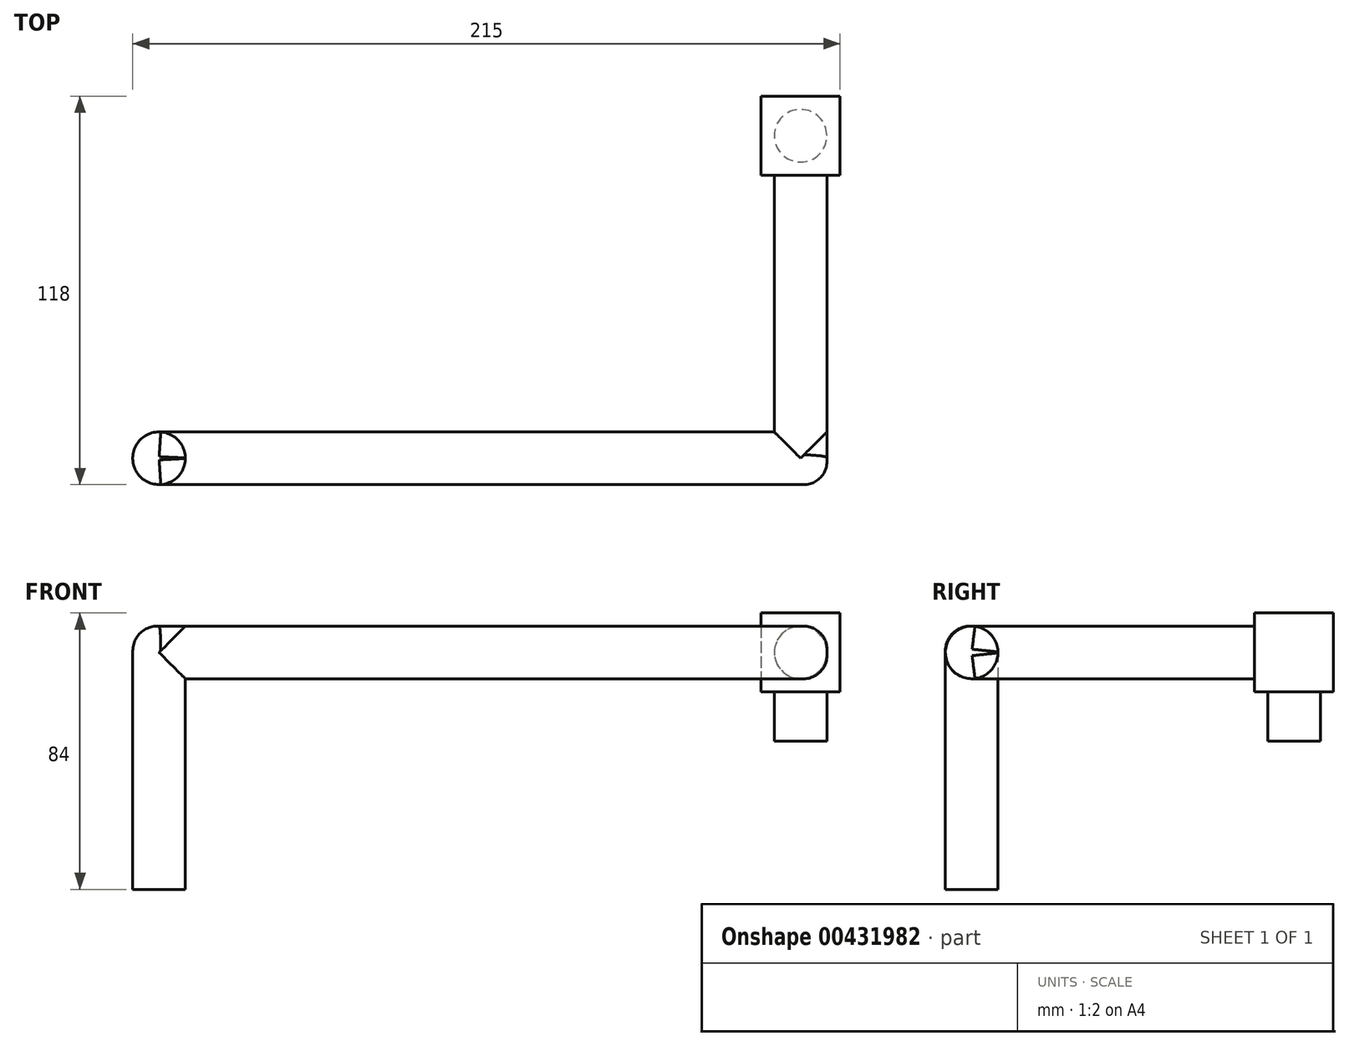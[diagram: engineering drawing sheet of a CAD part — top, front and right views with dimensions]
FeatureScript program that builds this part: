
annotation { "Feature Type Name" : "Feature", "Feature Type Description" : "" }
export const myFeature = defineFeature(function(context is Context, id is Id, definition is map)
    precondition{}
    {
        {
            var Q0;
            Q0=qCreatedBy(makeId("Top.planeOp"),FACE);
            var sketch = newSketch(context, id + "F0", { "sketchPlane" : qUnion([Q0])});
            skCircle(sketch, "E0", {"center": v(0, 0) * mm, "radius": 8 * mm});
            skSolve(sketch);
        }
        {
            var Q0;
            Q0=qSketchRegion(id+"F0",true);
            extrude(context, id + "F1", {"entities" : qUnion([Q0]), "depth" : 80 * mm});
        }
        {
            var Q0;
            Q0=qCreatedBy(makeId("Right.planeOp"),FACE);
            var sketch = newSketch(context, id + "F2", { "sketchPlane" : qUnion([Q0])});
            skCircle(sketch, "E1", {"center": v(0, 72) * mm, "radius": 8 * mm});
            skSolve(sketch);
        }
        {
            var Q0;
            Q0=qSketchRegion(id+"F2",true);
            extrude(context, id + "F3", {"entities" : qUnion([Q0]), "operationType" : NewBodyOperationType.ADD, "depth" : 203 * mm});
        }
        {
            var Q0;
            Q0=makeQuery(id+"F1.opExtrude","CAP_EDGE",EDGE,{"disambiguationData":[OSD([sQuery(id+"F0.wireOp",EDGE,"E0")])],"isStart":false});
            fillet(context, id + "F4", {"entities" : qUnion([Q0]), "radius" : 7.5 * mm, "tangentPropagation" : true, "allowEdgeOverflow" : false});
        }
        {
            var Q0;
            Q0=qCreatedBy(makeId("Front.planeOp"),FACE);
            var sketch = newSketch(context, id + "F5", { "sketchPlane" : qUnion([Q0])});
            skCircle(sketch, "E2", {"center": v(195, 72) * mm, "radius": 8 * mm});
            skLineSegment(sketch, "E3.0", {"start": v(203, 80) * mm, "end": v(203, 64) * mm, "construction": true});
            skLineSegment(sketch, "E4", {"start": v(195, 72) * mm, "end": v(203, 72) * mm, "construction": true});
            skSolve(sketch);
        }
        {
            var Q0;
            Q0=makeQuery(id+"F5.imprint","IMPRINT",FACE,{"disambiguationData":[TD([[makeQuery(id+"F5.imprint","IMPRINT",EDGE,{"derivedFrom":sQuery(id+"F5.wireOp",EDGE,"E2")}),1.0]])]});
            extrude(context, id + "F6", {"entities" : qUnion([Q0]), "operationType" : NewBodyOperationType.ADD, "oppositeDirection" : true, "depth" : 86 * mm});
        }
        {
            var Q0;
            Q0=makeQuery(id+"F3.opExtrude","CAP_EDGE",EDGE,{"disambiguationData":[OSD([sQuery(id+"F2.wireOp",EDGE,"E1")])],"isStart":false});
            fillet(context, id + "F7", {"entities" : qUnion([Q0]), "radius" : 7 * mm, "tangentPropagation" : true, "allowEdgeOverflow" : false});
        }
        {
            var Q0;
            Q0=makeQuery(id+"F6.opExtrude","CAP_FACE",FACE,{"disambiguationData":[OSD([sQuery(id+"F5.wireOp",EDGE,"E2")])],"isStart":false});
            var sketch = newSketch(context, id + "F8", { "sketchPlane" : qUnion([Q0])});
            skLineSegment(sketch, "E5.bottom", {"start": v(-183, 84) * mm, "end": v(-207, 84) * mm});
            skLineSegment(sketch, "E5.top", {"start": v(-183, 60) * mm, "end": v(-207, 60) * mm});
            skLineSegment(sketch, "E5.left", {"start": v(-183, 84) * mm, "end": v(-183, 60) * mm});
            skLineSegment(sketch, "E5.right", {"start": v(-207, 84) * mm, "end": v(-207, 60) * mm});
            skPoint(sketch, "E5.middle", {"position": v(-195, 72) * mm});
            skSolve(sketch);
        }
        {
            var Q0;
            Q0=qSketchRegion(id+"F8",true);
            extrude(context, id + "F9", {"entities" : qUnion([Q0]), "operationType" : NewBodyOperationType.ADD, "depth" : 24 * mm});
        }
        {
            var Q0;
            Q0=makeQuery(id+"F9.opExtrude","SWEPT_FACE",FACE,{"disambiguationData":[OSD([sQuery(id+"F8.wireOp",EDGE,"E5.top")])]});
            var sketch = newSketch(context, id + "F10", { "sketchPlane" : qUnion([Q0])});
            skCircle(sketch, "E6", {"center": v(195, -98) * mm, "radius": 8 * mm});
            skPoint(sketch, "E6.centerSnap0", {"position": v(195, -110) * mm});
            skPoint(sketch, "E6.centerSnap1", {"position": v(207, -98) * mm});
            skSolve(sketch);
        }
        {
            var Q0;
            Q0=qSketchRegion(id+"F10",true);
            extrude(context, id + "F11", {"entities" : qUnion([Q0]), "operationType" : NewBodyOperationType.ADD, "depth" : 15 * mm});
        }
    });
